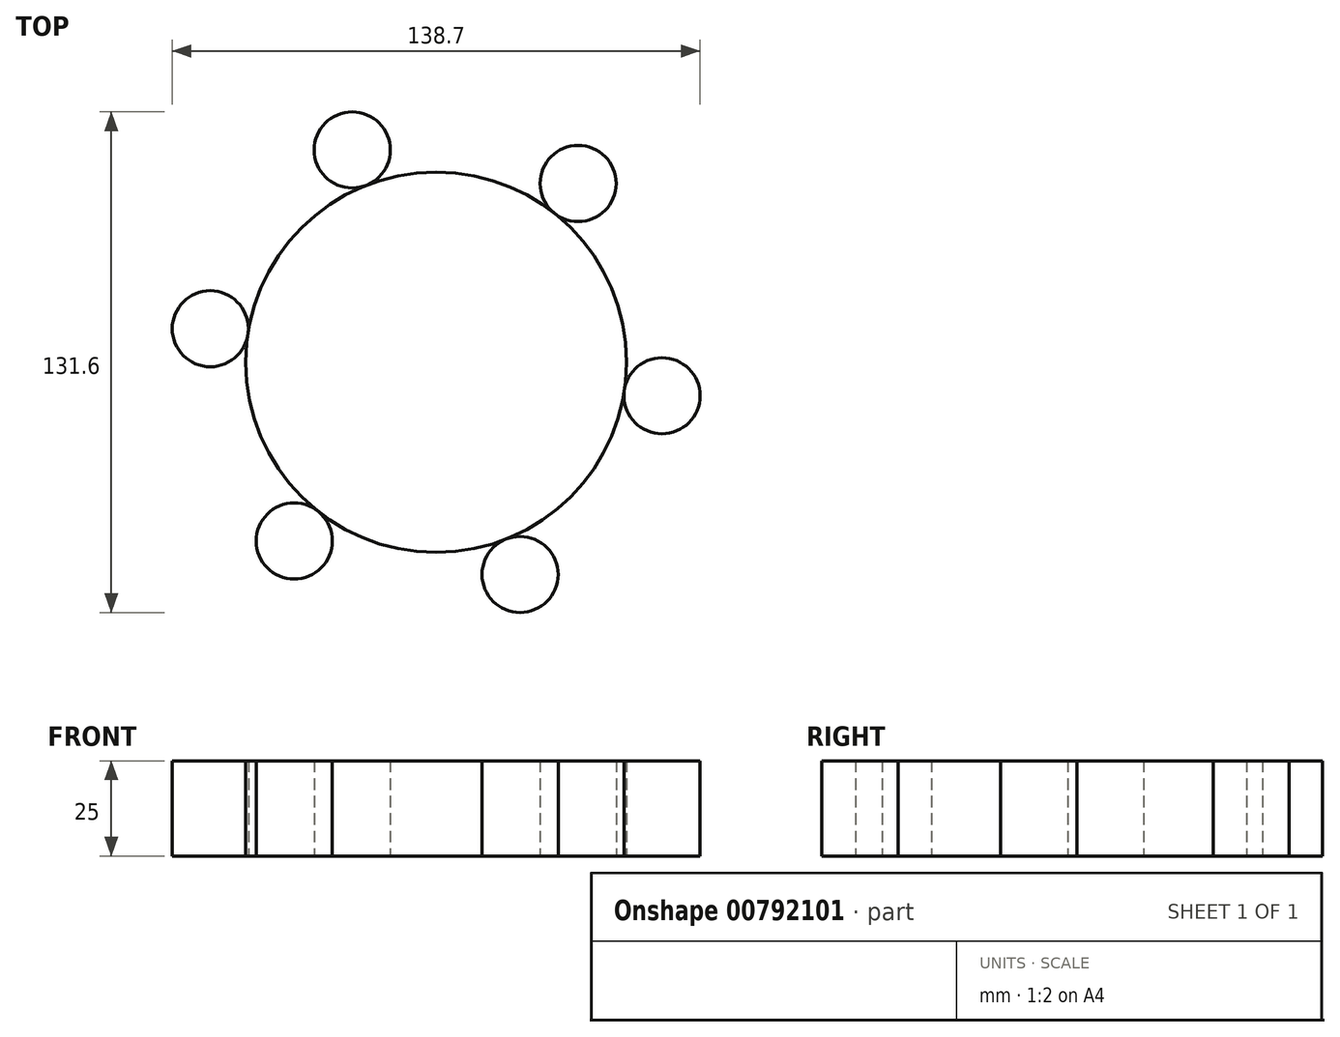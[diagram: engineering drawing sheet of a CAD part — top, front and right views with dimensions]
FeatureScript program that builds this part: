
annotation { "Feature Type Name" : "Feature", "Feature Type Description" : "" }
export const myFeature = defineFeature(function(context is Context, id is Id, definition is map)
    precondition{}
    {
        {
            var Q0;
            Q0=qCreatedBy(makeId("Top.planeOp"),FACE);
            var sketch = newSketch(context, id + "F0", { "sketchPlane" : qUnion([Q0])});
            skCircle(sketch, "E0", {"center": v(0, 0) * mm, "radius": 50 * mm});
            skCircle(sketch, "E1", {"center": v(22.05, -55.8) * mm, "radius": 10 * mm});
            skSolve(sketch);
        }
        {
            var Q0;
            {var subQ0=sQuery(id+"F0.wireOp",EDGE,"E0");Q0=makeQuery(id+"F0.imprint","IMPRINT",FACE,{"disambiguationData":[TD([[makeQuery(id+"F0.imprint","IMPRINT",EDGE,{"disambiguationData":[TD([[makeQuery(id+"F0.imprint","INTERSECT",VERTEX,{"derivedFrom":[subQ0,sQuery(id+"F0.wireOp",EDGE,"E1")]}),-1.0]])],"derivedFrom":subQ0}),1.0]])]});}
            var Q1;
            {var subQ0=sQuery(id+"F0.wireOp",EDGE,"E1");Q1=makeQuery(id+"F0.imprint","IMPRINT",FACE,{"disambiguationData":[TD([[makeQuery(id+"F0.imprint","IMPRINT",EDGE,{"disambiguationData":[TD([[makeQuery(id+"F0.imprint","INTERSECT",VERTEX,{"derivedFrom":[sQuery(id+"F0.wireOp",EDGE,"E0"),subQ0]}),-1.0]])],"derivedFrom":subQ0}),1.0]])]});}
            extrude(context, id + "F1", {"entities" : qUnion([Q0, Q1]), "depth" : 25 * mm, "offsetDistance" : 25 * mm});
        }
        {
            var Q0;
            Q0=makeQuery(id+"F1.opExtrude","SWEPT_BODY",BODY,{"disambiguationData":[OSD([sQuery(id+"F0.wireOp",EDGE,"E1")])]});
            var Q1;
            Q1=makeQuery(id+"F1.opExtrude","CAP_EDGE",EDGE,{"disambiguationData":[OSD([sQuery(id+"F0.wireOp",EDGE,"E0")])],"isStart":false});
            circularPattern(context, id + "F2", {"entities" : qUnion([Q0]), "axis" : qUnion([Q1]), "angle" : 360 * degree, "instanceCount" : 6, "equalSpace" : true});
        }
    });
